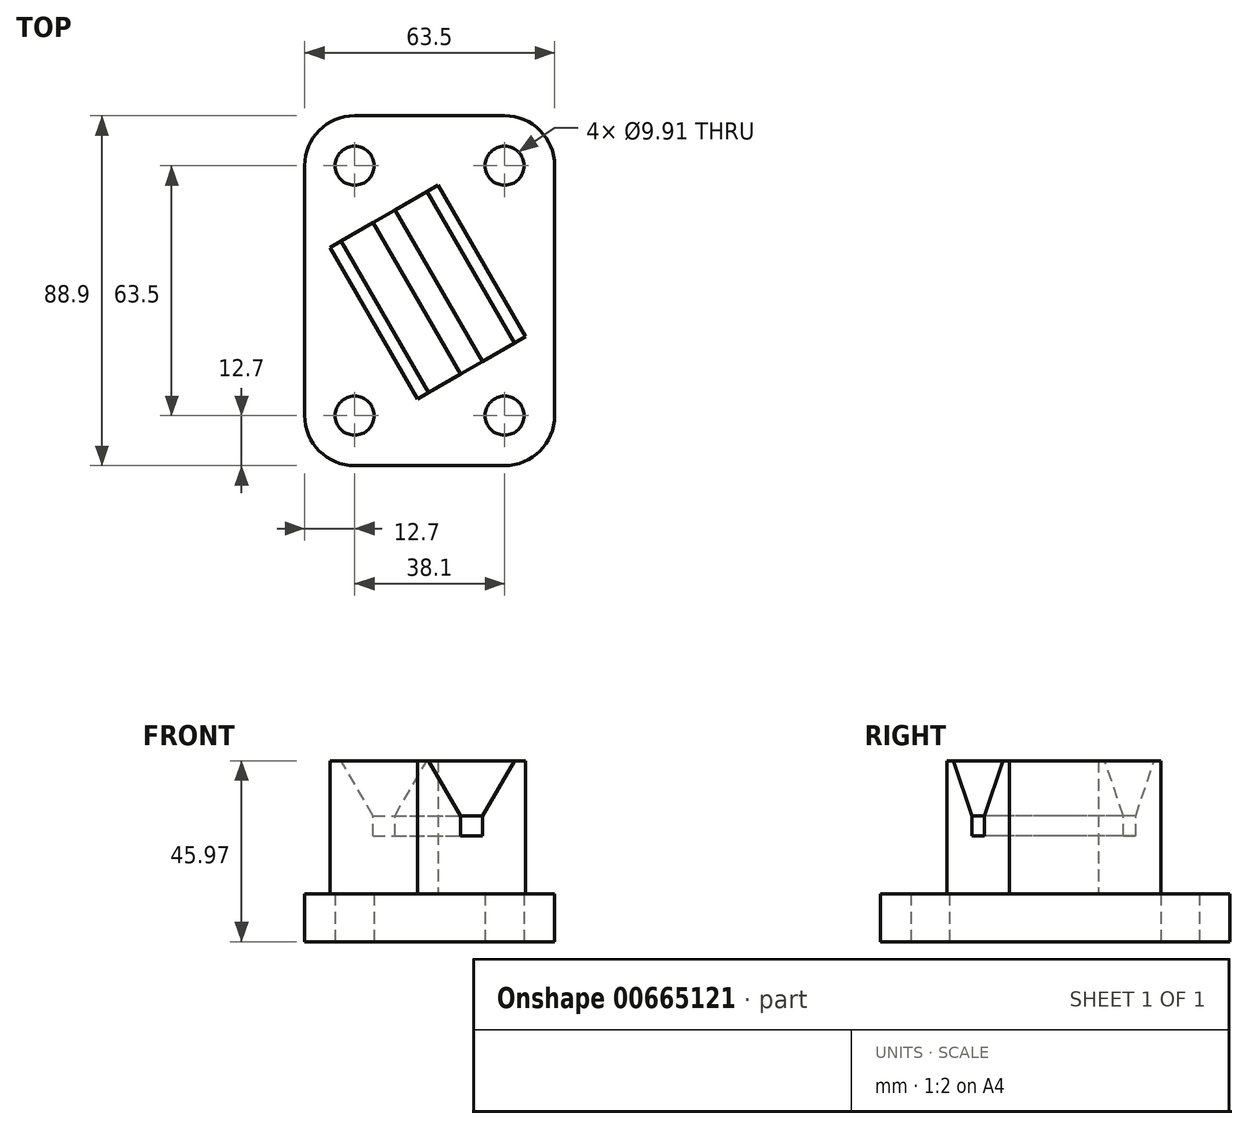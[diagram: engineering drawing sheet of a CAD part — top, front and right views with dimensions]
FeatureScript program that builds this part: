
annotation { "Feature Type Name" : "Feature", "Feature Type Description" : "" }
export const myFeature = defineFeature(function(context is Context, id is Id, definition is map)
    precondition{}
    {
        {
            var Q0;
            Q0=qCreatedBy(makeId("Top.planeOp"),FACE);
            var sketch = newSketch(context, id + "F0", { "sketchPlane" : qUnion([Q0])});
            skLineSegment(sketch, "E0", {"start": v(12.7, 0) * mm, "end": v(50.8, 0) * mm});
            skLineSegment(sketch, "E1", {"start": v(63.5, -12.7) * mm, "end": v(63.5, -76.2) * mm});
            skLineSegment(sketch, "E2", {"start": v(50.8, -88.9) * mm, "end": v(12.7, -88.9) * mm});
            skLineSegment(sketch, "E3", {"start": v(0, -76.2) * mm, "end": v(0, -12.7) * mm});
            skPoint(sketch, "E4.visualSharp", {"position": v(0, 0) * mm});
            skArc(sketch, "E4.filletArc", {"start": v(12.7, 0) * mm, "mid": v(3.72, -3.72) * mm, "end": v(0, -12.7) * mm});
            skPoint(sketch, "E5.visualSharp", {"position": v(63.5, 0) * mm});
            skArc(sketch, "E5.filletArc", {"start": v(63.5, -12.7) * mm, "mid": v(59.78, -3.72) * mm, "end": v(50.8, 0) * mm});
            skPoint(sketch, "E6.visualSharp", {"position": v(63.5, -88.9) * mm});
            skArc(sketch, "E6.filletArc", {"start": v(50.8, -88.9) * mm, "mid": v(59.78, -85.18) * mm, "end": v(63.5, -76.2) * mm});
            skPoint(sketch, "E7.visualSharp", {"position": v(0, -88.9) * mm});
            skArc(sketch, "E7.filletArc", {"start": v(0, -76.2) * mm, "mid": v(3.72, -85.18) * mm, "end": v(12.7, -88.9) * mm});
            skCircle(sketch, "E8", {"center": v(12.7, -12.7) * mm, "radius": 4.95 * mm});
            skCircle(sketch, "E9", {"center": v(50.8, -12.7) * mm, "radius": 4.95 * mm});
            skCircle(sketch, "E10", {"center": v(50.8, -76.2) * mm, "radius": 4.95 * mm});
            skCircle(sketch, "E11", {"center": v(12.7, -76.2) * mm, "radius": 4.95 * mm});
            skSolve(sketch);
        }
        {
            var Q0;
            Q0=makeQuery(id+"F0.imprint","IMPRINT",FACE,{"disambiguationData":[TD([[makeQuery(id+"F0.imprint","IMPRINT",EDGE,{"derivedFrom":sQuery(id+"F0.wireOp",EDGE,"E0")}),-1.0]])]});
            extrude(context, id + "F1", {"entities" : qUnion([Q0]), "depth" : 12.2 * mm, "offsetDistance" : 25.4 * mm});
        }
        {
            var Q0;
            Q0=makeQuery(id+"F1.opExtrude","CAP_FACE",FACE,{"disambiguationData":[OSD([sQuery(id+"F0.wireOp",EDGE,"E0"),sQuery(id+"F0.wireOp",EDGE,"E1"),sQuery(id+"F0.wireOp",EDGE,"E2"),sQuery(id+"F0.wireOp",EDGE,"E3"),sQuery(id+"F0.wireOp",EDGE,"E4.filletArc"),sQuery(id+"F0.wireOp",EDGE,"E5.filletArc"),sQuery(id+"F0.wireOp",EDGE,"E6.filletArc"),sQuery(id+"F0.wireOp",EDGE,"E7.filletArc"),sQuery(id+"F0.wireOp",EDGE,"E8"),sQuery(id+"F0.wireOp",EDGE,"E9"),sQuery(id+"F0.wireOp",EDGE,"E10"),sQuery(id+"F0.wireOp",EDGE,"E11")])],"isStart":false});
            var sketch = newSketch(context, id + "F2", { "sketchPlane" : qUnion([Q0])});
            skLineSegment(sketch, "E12", {"start": v(28.64, -72) * mm, "end": v(56.13, -56.13) * mm});
            skLineSegment(sketch, "E13", {"start": v(56.13, -56.13) * mm, "end": v(33.9, -17.64) * mm});
            skLineSegment(sketch, "E14", {"start": v(33.9, -17.64) * mm, "end": v(6.41, -33.51) * mm});
            skLineSegment(sketch, "E15", {"start": v(6.41, -33.51) * mm, "end": v(28.64, -72) * mm});
            skSolve(sketch);
        }
        {
            var Q0;
            Q0=makeQuery(id+"F2.imprint","IMPRINT",FACE,{"disambiguationData":[TD([[makeQuery(id+"F2.imprint","IMPRINT",EDGE,{"derivedFrom":sQuery(id+"F2.wireOp",EDGE,"E12")}),1.0]])]});
            extrude(context, id + "F3", {"entities" : qUnion([Q0]), "operationType" : NewBodyOperationType.ADD, "depth" : 33.78 * mm, "offsetDistance" : 25.4 * mm});
        }
        {
            var Q0;
            Q0=makeQuery(id+"F3.opExtrude","SWEPT_FACE",FACE,{"disambiguationData":[OSD([sQuery(id+"F2.wireOp",EDGE,"E12")])]});
            var sketch = newSketch(context, id + "F4", { "sketchPlane" : qUnion([Q0])});
            skLineSegment(sketch, "E16", {"start": v(-11.2, 45.97) * mm, "end": v(-7.9, 45.97) * mm});
            skLineSegment(sketch, "E17", {"start": v(20.55, 45.97) * mm, "end": v(17.24, 45.97) * mm});
            skLineSegment(sketch, "E18", {"start": v(17.24, 45.97) * mm, "end": v(17.24, 26.92) * mm});
            skLineSegment(sketch, "E19", {"start": v(-11.2, 45.97) * mm, "end": v(-11.2, 26.92) * mm});
            skLineSegment(sketch, "E20", {"start": v(-11.2, 26.92) * mm, "end": v(1.5, 26.92) * mm});
            skLineSegment(sketch, "E21", {"start": v(1.5, 26.92) * mm, "end": v(7.85, 26.92) * mm});
            skLineSegment(sketch, "E22", {"start": v(7.85, 26.92) * mm, "end": v(20.55, 26.92) * mm});
            skLineSegment(sketch, "E23", {"start": v(1.5, 26.92) * mm, "end": v(1.5, 32) * mm});
            skLineSegment(sketch, "E24", {"start": v(7.85, 26.92) * mm, "end": v(7.85, 32) * mm});
            skLineSegment(sketch, "E25", {"start": v(7.85, 32) * mm, "end": v(17.24, 45.97) * mm});
            skLineSegment(sketch, "E26", {"start": v(1.5, 32) * mm, "end": v(-7.9, 45.97) * mm});
            skSolve(sketch);
        }
        {
            var Q0;
            Q0=makeQuery(id+"F4.imprint","IMPRINT",FACE,{"disambiguationData":[TD([[makeQuery(id+"F4.imprint","IMPRINT",EDGE,{"derivedFrom":sQuery(id+"F4.wireOp",EDGE,"E21")}),1.0]])]});
            extrude(context, id + "F5", {"entities" : qUnion([Q0]), "operationType" : NewBodyOperationType.REMOVE, "oppositeDirection" : true, "depth" : 44.45 * mm, "offsetDistance" : 25.4 * mm});
        }
    });
